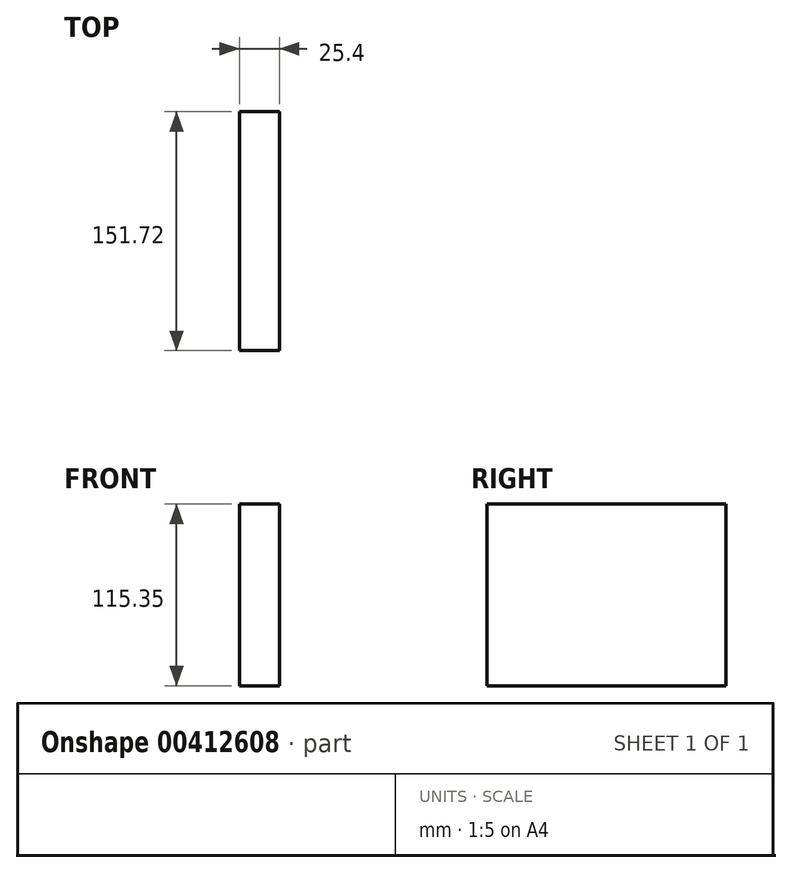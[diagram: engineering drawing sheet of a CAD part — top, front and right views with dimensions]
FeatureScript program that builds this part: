
annotation { "Feature Type Name" : "Feature", "Feature Type Description" : "" }
export const myFeature = defineFeature(function(context is Context, id is Id, definition is map)
    precondition{}
    {
        {
            var Q0;
            Q0=qCreatedBy(makeId("Right.planeOp"),FACE);
            var sketch = newSketch(context, id + "F0", { "sketchPlane" : qUnion([Q0])});
            skLineSegment(sketch, "E0.bottom", {"start": v(-39.56, 0) * mm, "end": v(112.16, 0) * mm});
            skLineSegment(sketch, "E0.top", {"start": v(-39.56, -115.35) * mm, "end": v(112.16, -115.35) * mm});
            skLineSegment(sketch, "E0.left", {"start": v(-39.56, 0) * mm, "end": v(-39.56, -115.35) * mm});
            skLineSegment(sketch, "E0.right", {"start": v(112.16, 0) * mm, "end": v(112.16, -115.35) * mm});
            skSolve(sketch);
        }
        {
            var Q0;
            Q0=makeQuery(id+"F0.imprint","IMPRINT",FACE,{"disambiguationData":[TD([[makeQuery(id+"F0.imprint","IMPRINT",EDGE,{"derivedFrom":sQuery(id+"F0.wireOp",EDGE,"E0.bottom")}),-1.0]])]});
            extrude(context, id + "F1", {"entities" : qUnion([Q0]), "depth" : 25.4 * mm});
        }
    });
